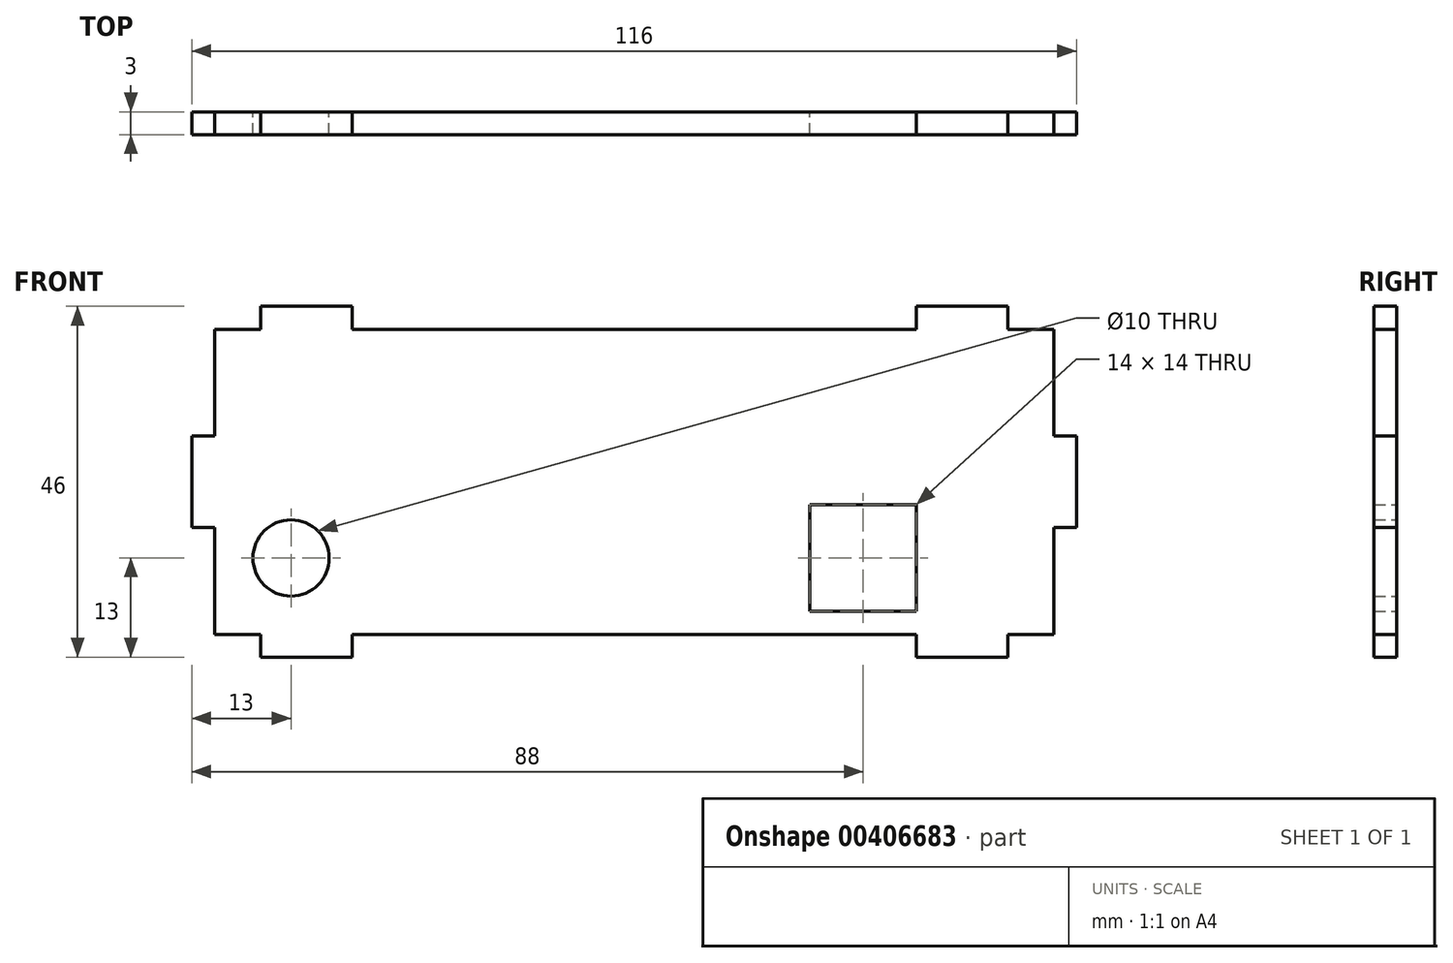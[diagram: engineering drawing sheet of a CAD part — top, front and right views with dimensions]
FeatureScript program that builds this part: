
annotation { "Feature Type Name" : "Feature", "Feature Type Description" : "" }
export const myFeature = defineFeature(function(context is Context, id is Id, definition is map)
    precondition{}
    {
        {
            var Q0;
            Q0=qCreatedBy(makeId("Front.planeOp"),FACE);
            var sketch = newSketch(context, id + "F0", { "sketchPlane" : qUnion([Q0])});
            skLineSegment(sketch, "E0.bottom", {"start": v(55, 20) * mm, "end": v(49, 20) * mm});
            skLineSegment(sketch, "E0.top", {"start": v(55, -20) * mm, "end": v(49, -20) * mm});
            skLineSegment(sketch, "E0.left", {"start": v(55, 20) * mm, "end": v(55, 6) * mm});
            skLineSegment(sketch, "E0.right", {"start": v(-55, 20) * mm, "end": v(-55, 6) * mm});
            skPoint(sketch, "E0.middle", {"position": v(0, 0) * mm});
            skLineSegment(sketch, "E1.top", {"start": v(-49, 23) * mm, "end": v(-37, 23) * mm});
            skLineSegment(sketch, "E1.left", {"start": v(-49, 20) * mm, "end": v(-49, 23) * mm});
            skLineSegment(sketch, "E1.right", {"start": v(-37, 20) * mm, "end": v(-37, 23) * mm});
            skLineSegment(sketch, "E2.bottom", {"start": v(-55, 6) * mm, "end": v(-58, 6) * mm});
            skLineSegment(sketch, "E2.top", {"start": v(-55, -6) * mm, "end": v(-58, -6) * mm});
            skLineSegment(sketch, "E2.right", {"start": v(-58, 6) * mm, "end": v(-58, -6) * mm});
            skLineSegment(sketch, "E3", {"start": v(0, 0) * mm, "end": v(0, 13.03) * mm, "construction": true});
            skLineSegment(sketch, "E4", {"start": v(0, 0) * mm, "end": v(-9.19, 0) * mm, "construction": true});
            skLineSegment(sketch, "E5.trimOffspring", {"start": v(-49, 20) * mm, "end": v(-55, 20) * mm});
            skLineSegment(sketch, "E6.trimOffspring", {"start": v(-55, -6) * mm, "end": v(-55, -20) * mm});
            skLineSegment(sketch, "E7.MirrorCS", {"start": v(-37, -20) * mm, "end": v(-37, -23) * mm});
            skLineSegment(sketch, "E8.MirrorCS", {"start": v(-49, -23) * mm, "end": v(-37, -23) * mm});
            skLineSegment(sketch, "E9.MirrorCS", {"start": v(-49, -20) * mm, "end": v(-49, -23) * mm});
            skLineSegment(sketch, "E10.MirrorCS", {"start": v(37, 20) * mm, "end": v(37, 23) * mm});
            skLineSegment(sketch, "E11.MirrorCS", {"start": v(49, 20) * mm, "end": v(49, 23) * mm});
            skLineSegment(sketch, "E12.MirrorCS", {"start": v(49, 23) * mm, "end": v(37, 23) * mm});
            skLineSegment(sketch, "E13.MirrorCS", {"start": v(37, -20) * mm, "end": v(37, -23) * mm});
            skLineSegment(sketch, "E14.MirrorCS", {"start": v(49, -23) * mm, "end": v(37, -23) * mm});
            skLineSegment(sketch, "E15.MirrorCS", {"start": v(49, -20) * mm, "end": v(49, -23) * mm});
            skLineSegment(sketch, "E16.MirrorCS", {"start": v(55, -6) * mm, "end": v(58, -6) * mm});
            skLineSegment(sketch, "E17.MirrorCS", {"start": v(55, 6) * mm, "end": v(58, 6) * mm});
            skLineSegment(sketch, "E18.MirrorCS", {"start": v(58, 6) * mm, "end": v(58, -6) * mm});
            skLineSegment(sketch, "E19.trimOffspring", {"start": v(37, 20) * mm, "end": v(-37, 20) * mm});
            skLineSegment(sketch, "E20.trimOffspring", {"start": v(55, -6) * mm, "end": v(55, -20) * mm});
            skLineSegment(sketch, "E21.trimOffspring", {"start": v(37, -20) * mm, "end": v(-37, -20) * mm});
            skLineSegment(sketch, "E22.trimOffspring", {"start": v(-49, -20) * mm, "end": v(-55, -20) * mm});
            skLineSegment(sketch, "E23.bottom", {"start": v(37, -17) * mm, "end": v(23, -17) * mm});
            skLineSegment(sketch, "E23.top", {"start": v(37, -3) * mm, "end": v(23, -3) * mm});
            skLineSegment(sketch, "E23.left", {"start": v(37, -17) * mm, "end": v(37, -3) * mm});
            skLineSegment(sketch, "E23.right", {"start": v(23, -17) * mm, "end": v(23, -3) * mm});
            skPoint(sketch, "E23.middle", {"position": v(30, -10) * mm});
            skCircle(sketch, "E24", {"center": v(-45, -10) * mm, "radius": 5 * mm});
            skSolve(sketch);
        }
        {
            var Q0;
            Q0=makeQuery(id+"F0.imprint","IMPRINT",FACE,{"disambiguationData":[TD([[makeQuery(id+"F0.imprint","IMPRINT",EDGE,{"derivedFrom":sQuery(id+"F0.wireOp",EDGE,"E0.bottom")}),1.0]])]});
            extrude(context, id + "F1", {"entities" : qUnion([Q0]), "depth" : 3 * mm});
        }
    });
